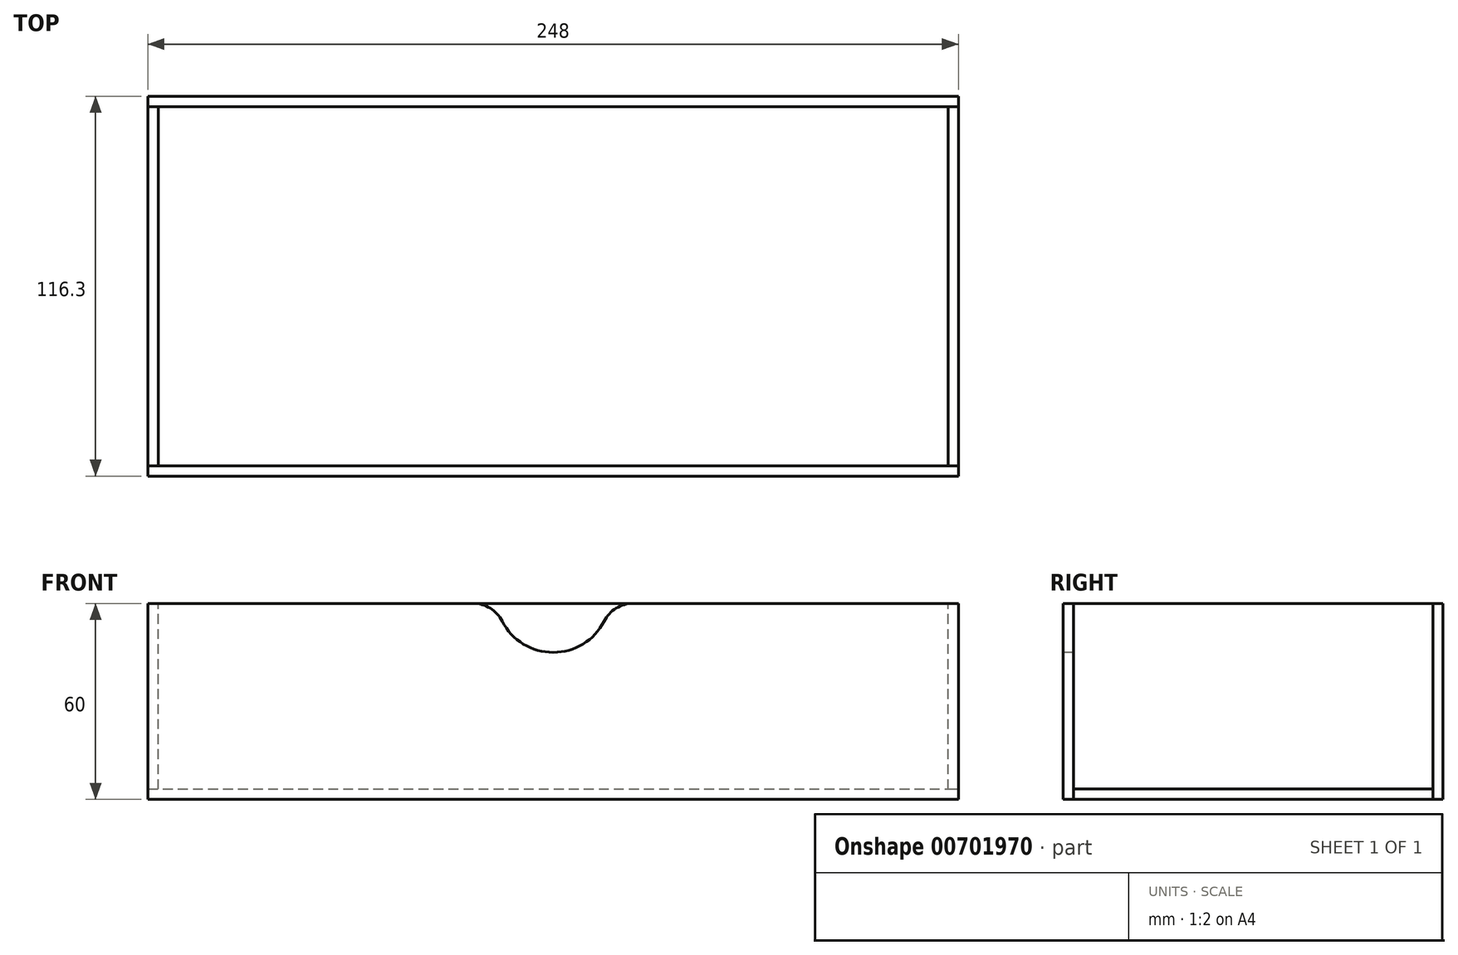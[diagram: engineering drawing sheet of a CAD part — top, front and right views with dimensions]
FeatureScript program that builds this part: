
annotation { "Feature Type Name" : "Feature", "Feature Type Description" : "" }
export const myFeature = defineFeature(function(context is Context, id is Id, definition is map)
    precondition{}
    {
        {
            assignVariable(context, id + "F0", {"name" : "x", "anyValue" : 3.15});
        }
        {
            var Q0;
            Q0=qCreatedBy(makeId("Front.planeOp"),FACE);
            var sketch = newSketch(context, id + "F1", { "sketchPlane" : qUnion([Q0])});
            skLineSegment(sketch, "E0.bottom", {"start": v(0, 0) * mm, "end": v(248, 0) * mm});
            skLineSegment(sketch, "E0.top", {"start": v(0, 60) * mm, "end": v(248, 60) * mm});
            skLineSegment(sketch, "E0.left", {"start": v(0, 0) * mm, "end": v(0, 60) * mm});
            skLineSegment(sketch, "E0.right", {"start": v(248, 0) * mm, "end": v(248, 60) * mm});
            skSolve(sketch);
        }
        {
            var Q0;
            Q0=qSketchRegion(id+"F1",true);
            extrude(context, id + "F2", {"entities" : qUnion([Q0]), "depth" : (getVariable(context, 'x')) * mm, "offsetDistance" : 25 * mm});
        }
        {
            var Q0;
            Q0=makeQuery(id+"F2.opExtrude","CAP_FACE",FACE,{"disambiguationData":[OSD([sQuery(id+"F1.wireOp",EDGE,"E0.bottom"),sQuery(id+"F1.wireOp",EDGE,"E0.top"),sQuery(id+"F1.wireOp",EDGE,"E0.left"),sQuery(id+"F1.wireOp",EDGE,"E0.right")])],"isStart":false});
            var sketch = newSketch(context, id + "F3", { "sketchPlane" : qUnion([Q0])});
            skCircle(sketch, "E1", {"center": v(124, 62.5) * mm, "radius": 17.5 * mm});
            skPoint(sketch, "E1.centerSnap0", {"position": v(124, 60) * mm});
            skSolve(sketch);
        }
        {
            var Q0;
            Q0=qSketchRegion(id+"F3",true);
            extrude(context, id + "F4", {"entities" : qUnion([Q0]), "operationType" : NewBodyOperationType.REMOVE, "oppositeDirection" : true, "depth" : 25 * mm, "offsetDistance" : 25 * mm});
        }
        {
            var Q0;
            Q0=makeQuery(id+"F4.boolean.opBoolean","INTERSECT",EDGE,{"disambiguationData":[OD(0.0)],"derivedFrom":[makeQuery(id+"FhRjEVInoXO9FZL_1.boolean.opBoolean","MERGE",FACE,{"derivedFrom":[makeQuery(id+"F2.opExtrude","SWEPT_FACE",FACE,{"disambiguationData":[OSD([sQuery(id+"F1.wireOp",EDGE,"E0.top")])]}),makeQuery(id+"FhRjEVInoXO9FZL_1.opExtrude","SWEPT_FACE",FACE,{"disambiguationData":[OSD([sQuery(id+"Fq4eTwGK3P5csYn_1.wireOp",EDGE,"AWsGmU2D-ZIxg-nKq1-UC4W-sWxty7mJGFEV")])]})]}),makeQuery(id+"F4.opExtrude","SWEPT_FACE",FACE,{"disambiguationData":[OSD([sQuery(id+"F3.wireOp",EDGE,"E1")])]})]});
            var Q1;
            Q1=makeQuery(id+"F4.boolean.opBoolean","INTERSECT",EDGE,{"disambiguationData":[OD(1.0)],"derivedFrom":[makeQuery(id+"FhRjEVInoXO9FZL_1.boolean.opBoolean","MERGE",FACE,{"derivedFrom":[makeQuery(id+"F2.opExtrude","SWEPT_FACE",FACE,{"disambiguationData":[OSD([sQuery(id+"F1.wireOp",EDGE,"E0.top")])]}),makeQuery(id+"FhRjEVInoXO9FZL_1.opExtrude","SWEPT_FACE",FACE,{"disambiguationData":[OSD([sQuery(id+"Fq4eTwGK3P5csYn_1.wireOp",EDGE,"AWsGmU2D-ZIxg-nKq1-UC4W-sWxty7mJGFEV")])]})]}),makeQuery(id+"F4.opExtrude","SWEPT_FACE",FACE,{"disambiguationData":[OSD([sQuery(id+"F3.wireOp",EDGE,"E1")])]})]});
            fillet(context, id + "F5", {"entities" : qUnion([Q0, Q1]), "radius" : 10 * mm, "tangentPropagation" : true, "allowEdgeOverflow" : false});
        }
        {
            var Q0;
            Q0=makeQuery(id+"F2.opExtrude","SWEPT_FACE",FACE,{"disambiguationData":[OSD([sQuery(id+"F1.wireOp",EDGE,"E0.right")])]});
            var sketch = newSketch(context, id + "F6", { "sketchPlane" : qUnion([Q0])});
            skLineSegment(sketch, "E2.bottom", {"start": v(0, 60) * mm, "end": v(110, 60) * mm});
            skLineSegment(sketch, "E2.top", {"start": v(0, 3.15) * mm, "end": v(110, 3.15) * mm});
            skLineSegment(sketch, "E2.left", {"start": v(0, 60) * mm, "end": v(0, 3.15) * mm});
            skLineSegment(sketch, "E2.right", {"start": v(110, 60) * mm, "end": v(110, 3.15) * mm});
            skSolve(sketch);
        }
        {
            var Q0;
            Q0=qSketchRegion(id+"F6",true);
            extrude(context, id + "F7", {"entities" : qUnion([Q0]), "oppositeDirection" : true, "depth" : (getVariable(context, 'x')) * mm, "offsetDistance" : 25 * mm});
        }
        {
            var Q0;
            Q0=makeQuery(id+"F7.opExtrude","SWEPT_BODY",BODY,{"disambiguationData":[OSD([sQuery(id+"F6.wireOp",EDGE,"E2.bottom"),sQuery(id+"F6.wireOp",EDGE,"E2.top"),sQuery(id+"F6.wireOp",EDGE,"E2.left"),sQuery(id+"F6.wireOp",EDGE,"E2.right")])]});
            transform(context, id + "F8", {"entities" : qUnion([Q0]), "transformType" : TransformType.TRANSLATION_3D, "dx" : (-248 + 3.15) * mm, "dy" : 0 * mm, "dz" : 0 * mm, "makeCopy" : true});
        }
        {
            var Q0;
            Q0=makeQuery(id+"F7.opExtrude","SWEPT_FACE",FACE,{"disambiguationData":[OSD([sQuery(id+"F6.wireOp",EDGE,"E2.right")])]});
            var sketch = newSketch(context, id + "F9", { "sketchPlane" : qUnion([Q0])});
            skLineSegment(sketch, "E3.bottom", {"start": v(-248, 60) * mm, "end": v(0, 60) * mm});
            skLineSegment(sketch, "E3.top", {"start": v(-248, 0) * mm, "end": v(0, 0) * mm});
            skLineSegment(sketch, "E3.left", {"start": v(-248, 60) * mm, "end": v(-248, 0) * mm});
            skLineSegment(sketch, "E3.right", {"start": v(0, 60) * mm, "end": v(0, 0) * mm});
            skSolve(sketch);
        }
        {
            var Q0;
            Q0=qSketchRegion(id+"F9",true);
            extrude(context, id + "F10", {"entities" : qUnion([Q0]), "depth" : (getVariable(context, 'x')) * mm, "offsetDistance" : 25 * mm});
        }
        {
            var Q0;
            Q0=makeQuery(id+"F8.opPattern","COPY",FACE,{"derivedFrom":makeQuery(id+"F7.opExtrude","SWEPT_FACE",FACE,{"disambiguationData":[OSD([sQuery(id+"F6.wireOp",EDGE,"E2.top")])]}),"instanceName":"1"});
            var sketch = newSketch(context, id + "F11", { "sketchPlane" : qUnion([Q0])});
            skLineSegment(sketch, "E4.bottom", {"start": v(0, 0) * mm, "end": v(248, 0) * mm});
            skLineSegment(sketch, "E4.top", {"start": v(0, -110) * mm, "end": v(248, -110) * mm});
            skLineSegment(sketch, "E4.left", {"start": v(0, 0) * mm, "end": v(0, -110) * mm});
            skLineSegment(sketch, "E4.right", {"start": v(248, 0) * mm, "end": v(248, -110) * mm});
            skSolve(sketch);
        }
        {
            var Q0;
            Q0=qSketchRegion(id+"F11",true);
            extrude(context, id + "F12", {"entities" : qUnion([Q0]), "depth" : (getVariable(context, 'x')) * mm, "offsetDistance" : 25 * mm});
        }
    });
